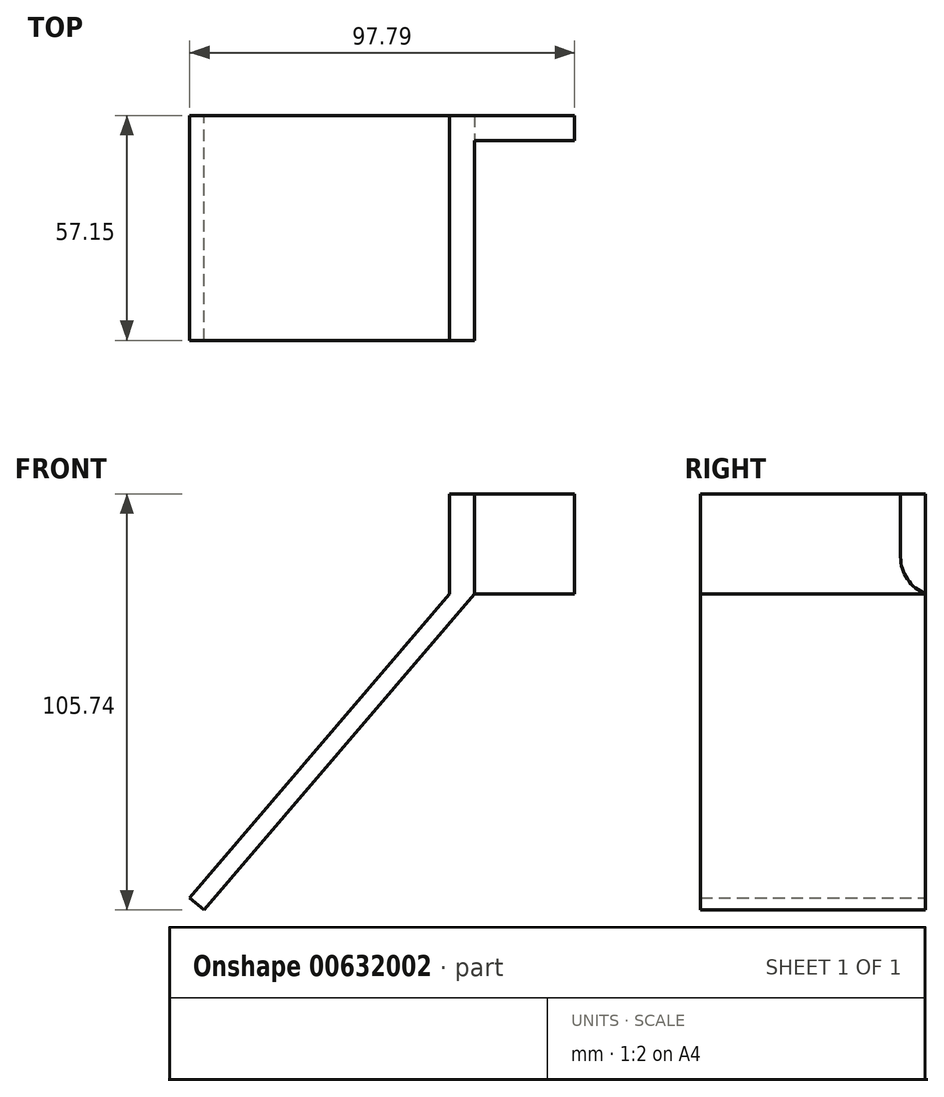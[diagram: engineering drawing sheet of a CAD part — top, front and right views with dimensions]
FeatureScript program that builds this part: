
annotation { "Feature Type Name" : "Feature", "Feature Type Description" : "" }
export const myFeature = defineFeature(function(context is Context, id is Id, definition is map)
    precondition{}
    {
        {
            var Q0;
            Q0=qCreatedBy(makeId("Front.planeOp"),FACE);
            var sketch = newSketch(context, id + "F0", { "sketchPlane" : qUnion([Q0])});
            skLineSegment(sketch, "E0", {"start": v(0, 25.4) * mm, "end": v(0, 0) * mm});
            skLineSegment(sketch, "E1", {"start": v(0, 0) * mm, "end": v(-66.04, -77.2) * mm});
            skLineSegment(sketch, "E2", {"start": v(-66.04, -77.2) * mm, "end": v(-62.38, -80.34) * mm});
            skLineSegment(sketch, "E3", {"start": v(-62.38, -80.34) * mm, "end": v(6.35, 0) * mm});
            skLineSegment(sketch, "E4", {"start": v(6.35, 0) * mm, "end": v(6.35, 25.4) * mm});
            skLineSegment(sketch, "E5", {"start": v(6.35, 25.4) * mm, "end": v(0, 25.4) * mm});
            skSolve(sketch);
        }
        {
            var Q0;
            Q0=makeQuery(id+"F0.imprint","IMPRINT",FACE,{"disambiguationData":[TD([[makeQuery(id+"F0.imprint","IMPRINT",EDGE,{"derivedFrom":sQuery(id+"F0.wireOp",EDGE,"E0")}),1.0]])]});
            extrude(context, id + "F1", {"entities" : qUnion([Q0]), "depth" : 57.15 * mm, "offsetDistance" : 25.4 * mm});
        }
        {
            var Q0;
            Q0=makeQuery(id+"F1.opExtrude","SWEPT_FACE",FACE,{"disambiguationData":[OSD([sQuery(id+"F0.wireOp",EDGE,"E4")])]});
            var sketch = newSketch(context, id + "F2", { "sketchPlane" : qUnion([Q0])});
            skLineSegment(sketch, "E6.bottom", {"start": v(0, 0) * mm, "end": v(-6.35, 0) * mm});
            skLineSegment(sketch, "E6.top", {"start": v(0, 25.4) * mm, "end": v(-6.35, 25.4) * mm});
            skLineSegment(sketch, "E6.left", {"start": v(0, 0) * mm, "end": v(0, 25.4) * mm});
            skLineSegment(sketch, "E6.right", {"start": v(-6.35, 0) * mm, "end": v(-6.35, 25.4) * mm});
            skSolve(sketch);
        }
        {
            var Q0;
            Q0=makeQuery(id+"F2.imprint","IMPRINT",FACE,{"disambiguationData":[TD([[makeQuery(id+"F2.imprint","IMPRINT",EDGE,{"derivedFrom":sQuery(id+"F2.wireOp",EDGE,"E6.bottom")}),1.0]])]});
            extrude(context, id + "F3", {"entities" : qUnion([Q0]), "operationType" : NewBodyOperationType.ADD, "depth" : 25.4 * mm, "offsetDistance" : 25.4 * mm});
        }
        {
            var Q0;
            Q0=makeQuery(id+"F3.opExtrude","SWEPT_EDGE",EDGE,{"disambiguationData":[OSD([sQuery(id+"F0.wireOp",EDGE,"E3"),sQuery(id+"F0.wireOp",EDGE,"E4"),sQuery(id+"F2.wireOp",EDGE,"E6.bottom"),sQuery(id+"F2.wireOp",EDGE,"E6.right")])]});
            fillet(context, id + "F4", {"entities" : qUnion([Q0]), "radius" : 10.16 * mm, "tangentPropagation" : true, "allowEdgeOverflow" : false});
        }
    });
